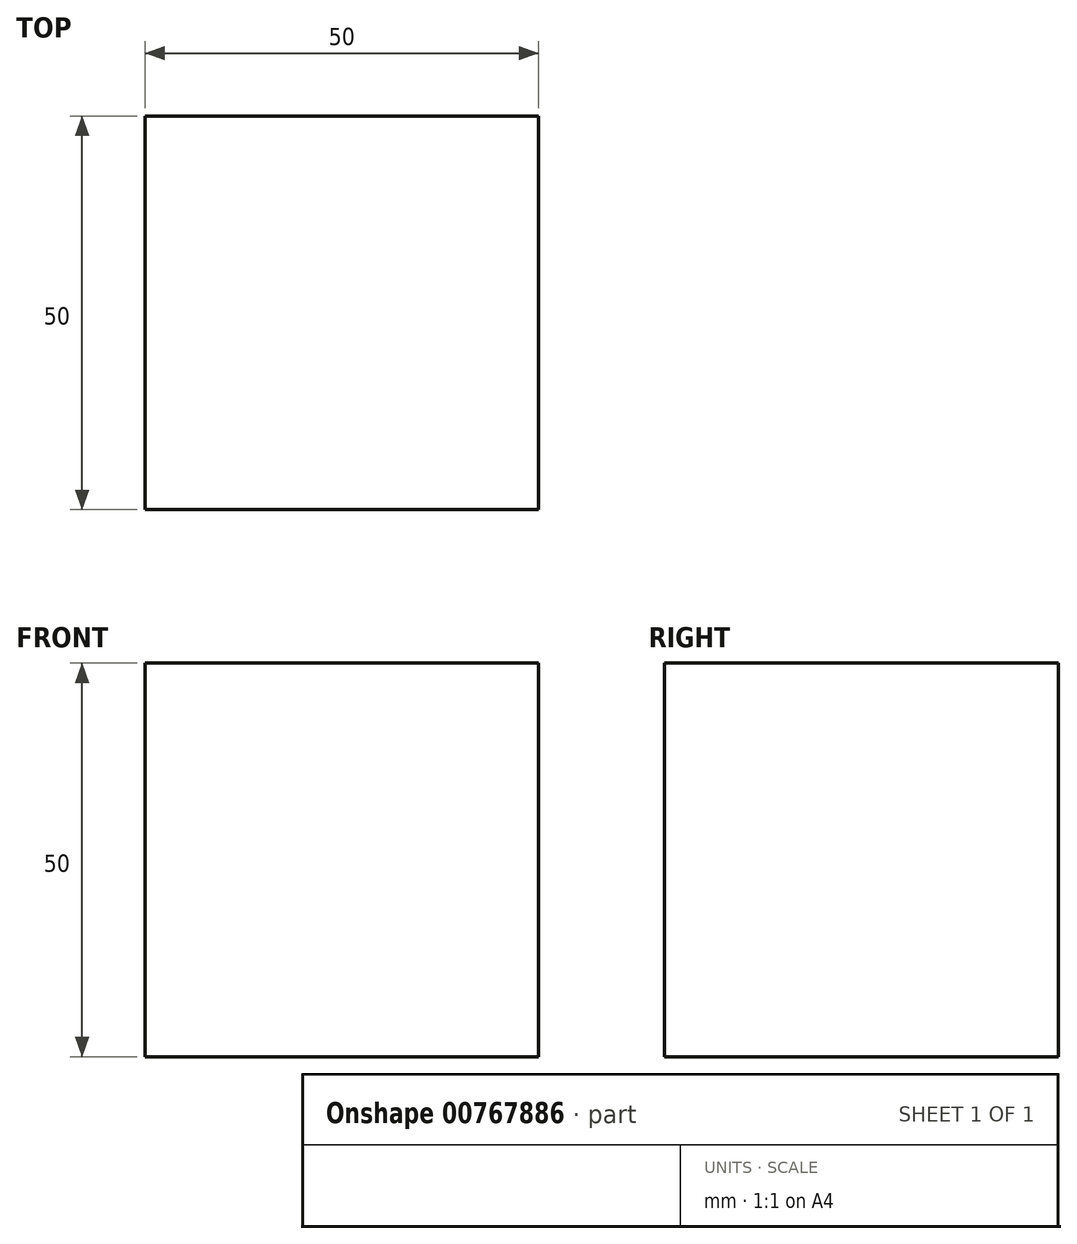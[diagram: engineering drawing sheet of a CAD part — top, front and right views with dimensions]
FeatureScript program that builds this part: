
annotation { "Feature Type Name" : "Feature", "Feature Type Description" : "" }
export const myFeature = defineFeature(function(context is Context, id is Id, definition is map)
    precondition{}
    {
        {
            var Q0;
            Q0=qCreatedBy(makeId("Top.planeOp"),FACE);
            var sketch = newSketch(context, id + "F0", { "sketchPlane" : qUnion([Q0])});
            skLineSegment(sketch, "E0.bottom", {"start": v(-25, 25) * mm, "end": v(25, 25) * mm});
            skLineSegment(sketch, "E0.top", {"start": v(-25, -25) * mm, "end": v(25, -25) * mm});
            skLineSegment(sketch, "E0.left", {"start": v(-25, 25) * mm, "end": v(-25, -25) * mm});
            skLineSegment(sketch, "E0.right", {"start": v(25, 25) * mm, "end": v(25, -25) * mm});
            skSolve(sketch);
        }
        {
            var Q0;
            Q0=makeQuery(id+"F0.imprint","IMPRINT",FACE,{"disambiguationData":[TD([[makeQuery(id+"F0.imprint","IMPRINT",EDGE,{"derivedFrom":sQuery(id+"F0.wireOp",EDGE,"E0.bottom")}),-1.0]])]});
            extrude(context, id + "F1", {"entities" : qUnion([Q0]), "depth" : 25 * mm, "offsetDistance" : 25 * mm, "hasSecondDirection" : true, "secondDirectionOppositeDirection" : true, "secondDirectionDepth" : 25 * mm});
        }
    });
